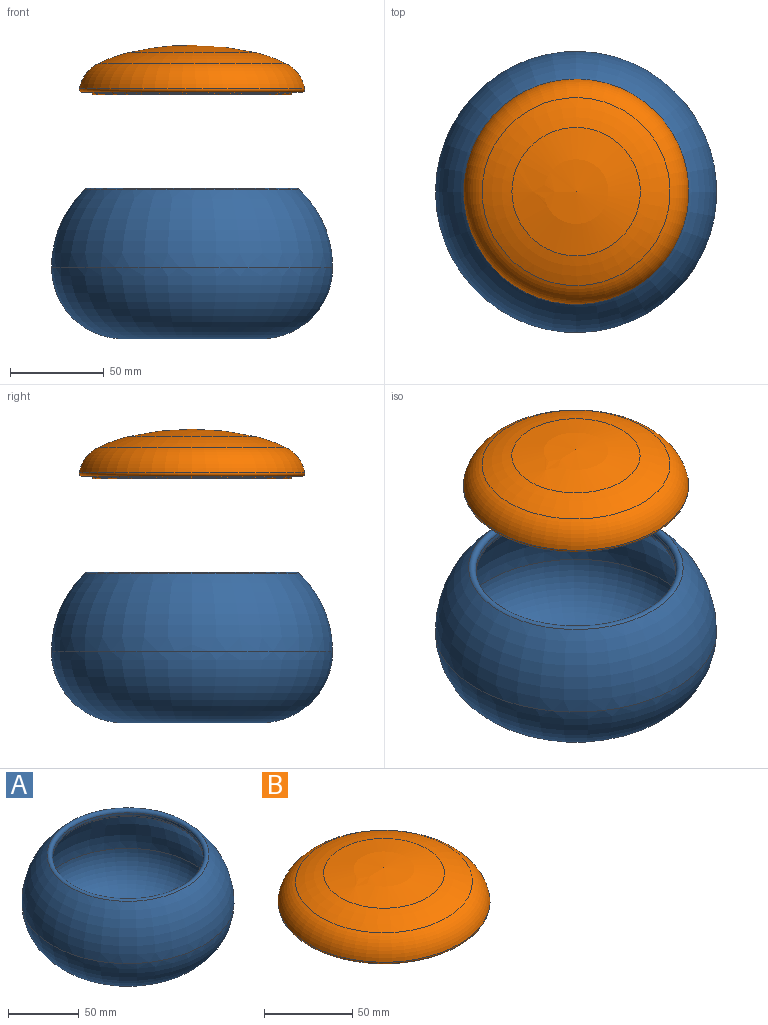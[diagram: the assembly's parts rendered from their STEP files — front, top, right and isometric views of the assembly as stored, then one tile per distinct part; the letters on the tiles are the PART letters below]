
ASSEMBLY  parts=2 mates=1
PART A: 9 faces, bbox 149.9x149.9x80.1 mm
  f0: torus R=55.63mm, axis (0,0,-1), area 1839.5mm2, adj f1,f8
  f1: cylinder r=53.34mm len=106.68mm, axis (0,0,-1), area 714.6mm2, adj f0,f2
  f2: torus R=55.63mm, axis (0,0,-1), area 500.7mm2, adj f1,f3
  f3: torus R=6.35mm, axis (0,0,-1), area 15129.3mm2, adj f2,f4
  f4: torus R=38.1mm, axis (0,0,-1), area 15411.3mm2, adj f3,f5
  f5: plane 76.2x76.2mm, normal (0,0,1), area 4560.4mm2, adj f4
  f6: plane 73.66x73.66mm, normal (0,0,-1), area 4261.4mm2, adj f7
  f7: torus R=36.83mm, axis (0,0,-1), area 22970mm2, adj f6,f8
  f8: torus R=17.78mm, axis (0,0,-1), area 20026.1mm2, adj f0,f7
PART B: 10 faces, bbox 130.6x130.6x26.3 mm
  f0: torus R=38.1mm, axis (0,0,-1), area 3928.7mm2, adj f1,f9
  f1: torus R=49.6mm, axis (0,0,-1), area 354.3mm2, adj f0,f2
  f2: plane 104.83x104.83mm, normal (0,0,-1), area 900.8mm2, adj f1,f3
  f3: torus R=52.41mm, axis (0,0,-1), area 338.5mm2, adj f2,f4
  f4: torus R=55.63mm, axis (0,0,-1), area 1882.6mm2, adj f3,f5
  f5: torus R=58.55mm, axis (0,0,-1), area 1437.4mm2, adj f4,f6
  f6: torus R=41.91mm, axis (0,0,-1), area 6121.2mm2, adj f5,f7
  f7: torus R=15.24mm, axis (0,0,-1), area 4495.6mm2, adj f6,f8
  f8: sphere r=146.96mm, area 3729.6mm2, adj f7
  f9: sphere r=177.75mm, area 5258.2mm2, adj f0
PLACE A t=(0,0,38.1)mm
PLACE B t=(0,0,-32.44)mm
MATE slider A.f0 <-> B.f0  axis (0,0,-1) through (0,0,0)mm
